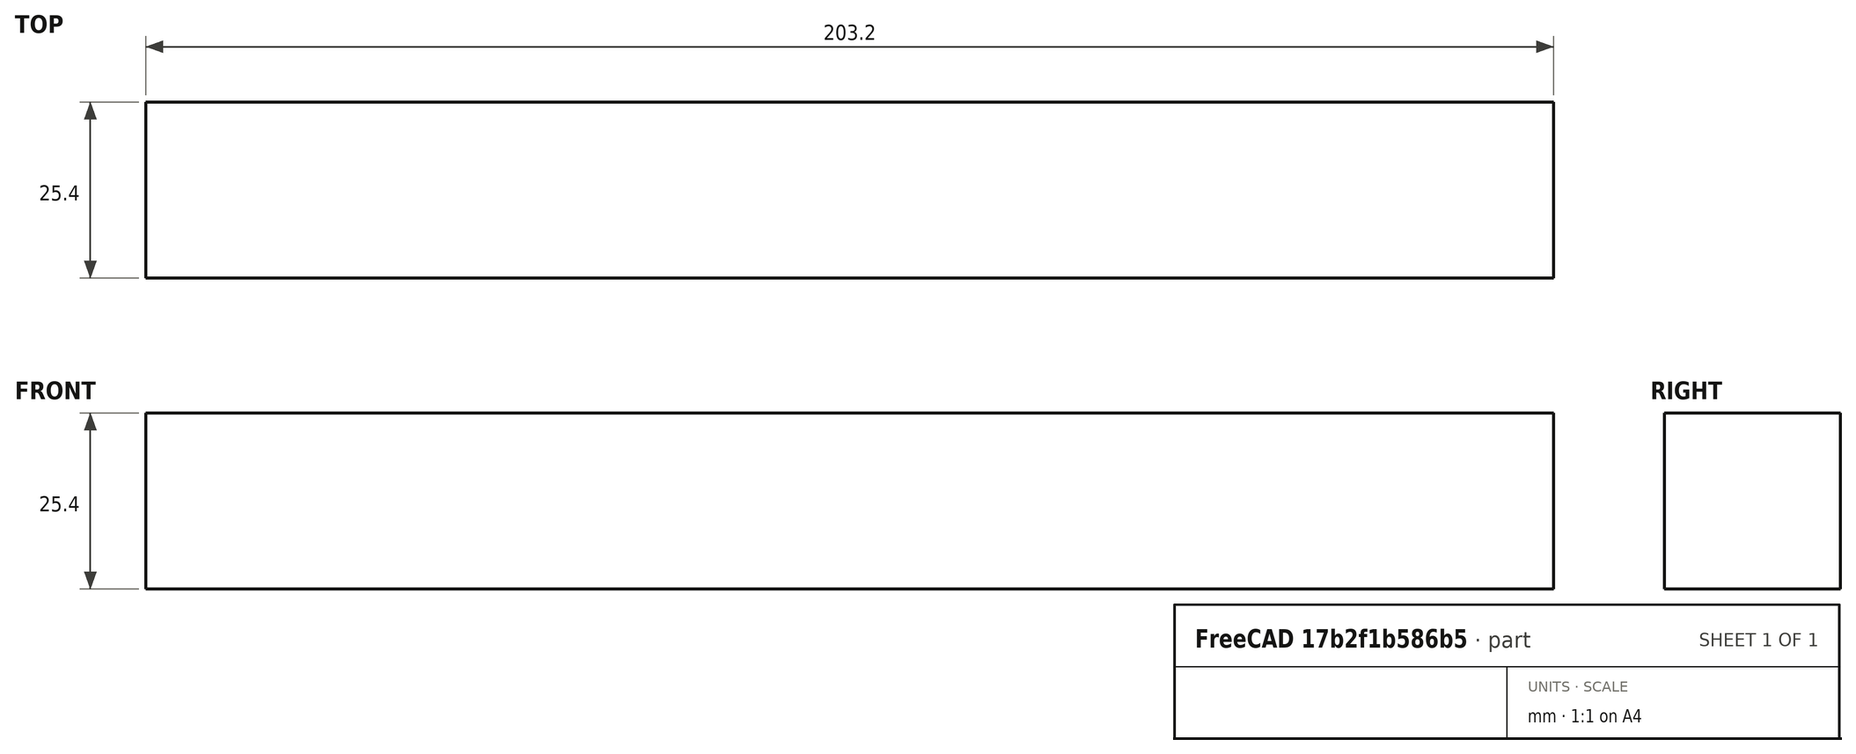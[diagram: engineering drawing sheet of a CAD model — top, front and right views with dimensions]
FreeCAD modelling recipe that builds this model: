
FCSTD DOCUMENT  (FreeCAD 0.17R10699 (Git))
Label: spine_thermomech
License: All rights reserved
LicenseURL: http://en.wikipedia.org/wiki/All_rights_reserved
objects: Part::Box×1, Fem::FemSolverObjectPython×1, Fem::FemMeshObject×1, App::MaterialObjectPython×1, Fem::ConstraintFixed×1, Fem::ConstraintInitialTemperature×1, Fem::ConstraintTemperature×1, Fem::ConstraintHeatflux×1, Fem::FemResultObjectPython×1, Fem::FemAnalysisPython×1
note: 1 computed .brp shape members not serialized (recipe doc carries the construction recipe); baked Part::Feature solids carry a one-line shape summary decoded from their .brp

FEATURE [Part::Box] Box
  AttacherType = Attacher::AttachEngine3D
  Height = 25.4
  Length = 203.2
  Width = 25.4
FEATURE [Fem::FemSolverObjectPython] CalculiX  # FEM object (typed FeaturePython)
  AnalysisType = 2
  EigenmodeHighLimit = 1000
  EigenmodeLowLimit = 0.5
  EigenmodesCount = 15
  GeometricalNonlinearity = 0
  IterationsControlParameterCutb = 0.25,0.5,0.75,0.85,,,1.5,
  IterationsControlParameterIter = 4,8,9,200,10,400,,200,,
  IterationsControlParameterTimeUse = true
  IterationsThermoMechMaximum = 2000
  IterationsUserDefinedIncrementations = false
  IterationsUserDefinedTimeStepLength = 0.1, 1.0
  MaterialNonlinearity = 0
  MatrixSolverType = 0
  SolverType = FemSolverCalculix
  SplitInputWriter = false
  ThermoMechSteadyState = true
  TimeEnd = 1
  TimeInitialStep = 1
FEATURE [Fem::FemMeshObject] Mesh
FEATURE [App::MaterialObjectPython] MechanicalMaterial  # material (typed FeaturePython)
  Category = 0
  Material = Density=7900 kg/m^3,Name=Steel-Generic,PoissonRatio=0.30,SpecificHeat=500 J/kg/K,ThermalConductivity=43.27 W/m/K,+2 more (map truncated)
FEATURE [Fem::ConstraintFixed] FemConstraintFixed
  NormalDirection = (-1,0,0)
  Normals = (16) [(-1,0,0),(-1,0,0),(-1,0,0),(-1,0,0),(-1,0,0),(-1,0,0),(-1,0,0),(-1,0,0),(-1,0,0),(-1,0,0),(-1,0,0),(-1,0,0),(-1,0,0),(-1,0,0),(-1,0,0),(-1,0,0)]
  Points = (16) [(0,25.4,0),(0,25.4,8.46667),(0,25.4,16.9333),(0,25.4,25.4),(0,16.9333,0),(0,16.9333,8.46667),(0,16.9333,16.9333),(0,16.9333,25.4),(0,8.46667,0),+7 more]
  References = -> [Box]
FEATURE [Fem::ConstraintInitialTemperature] FemConstraintInitialTemperature
  NormalDirection = (0,0,1)
  initialTemperature = 300
FEATURE [Fem::ConstraintTemperature] FemConstraintTemperature
  CFlux = 0
  ConstraintType = 1
  NormalDirection = (-1,0,0)
  Normals = (16) [(-1,0,0),(-1,0,0),(-1,0,0),(-1,0,0),(-1,0,0),(-1,0,0),(-1,0,0),(-1,0,0),(-1,0,0),(-1,0,0),(-1,0,0),(-1,0,0),(-1,0,0),(-1,0,0),(-1,0,0),(-1,0,0)]
  Points = (16) [(0,25.4,0),(0,25.4,8.46667),(0,25.4,16.9333),(0,25.4,25.4),(0,16.9333,0),(0,16.9333,8.46667),(0,16.9333,16.9333),(0,16.9333,25.4),(0,8.46667,0),+7 more]
  References = -> [Box]
  Temperature = 310.93
FEATURE [Fem::ConstraintHeatflux] FemConstraintHeatflux
  AmbientTemp = 255.372
  ConstraintType = 1
  DFlux = 0
  FilmCoef = 5.678
  NormalDirection = (0,-1,0)
  Normals = (64) [(0,-1,0),(0,-1,0),(0,-1,0),(0,-1,0),(0,-1,0),(0,-1,0),(0,-1,0),(0,-1,0),(0,-1,0),(0,-1,0),(0,-1,0),(0,-1,0),(0,-1,0),(0,-1,0),(0,-1,0),(0,-1,0),+48 more]
  Points = (64) [(0,0,0),(0,0,8.46667),(0,0,16.9333),(0,0,25.4),(67.7333,0,0),(67.7333,0,8.46667),(67.7333,0,16.9333),(67.7333,0,25.4),(135.467,0,0),+55 more]
  References = -> [Box]
  Scale = 11
FEATURE [Fem::FemResultObjectPython] CalculiX_thermomech_results  # FEM object (typed FeaturePython)
  DisplacementLengths = [0.00167108,0.0024824,0.00107755,0.00186939,0,0,0,0,0.00681127,0.00647907,0.00661732,0.00613781,0,0.00582005,0.00418411,0.00189581,0.00662788,0.00374675,0,0.00650644,0.00378478,0.0009262,0.00732571,0.0033935,0.00179715,0,0.00109313,0,0,+16 more]
  DisplacementVectors = (45) [(-0.000352892,-0.00160726,0.000290995),(0.000241406,-0.00163382,-0.00185329),(-0.000942455,0.00044281,0.00027714),+42 more]
  Eigenmode = 0
  EigenmodeFrequency = 0
  MaxShear = [0.309833,0.168182,0.472147,0.32241,15.4529,9.03465,18.1004,15.3132,0.781265,2.33473,2.32084,5.14995,14.7282,2.91877,0.45032,0.376204,4.16462,0.382447,17.032,4.1618,0.310077,0.482185,2.15922,0.408214,0.327898,14.8602,0.492202,17.4632,+17 more]
  Mesh = -> Mesh
  NodeNumbers = [1,2,3,4,5,6,7,8,9,10,11,12,13,14,15,16,17,18,19,20,21,22,23,24,25,26,27,28,29,30,31,32,33,34,35,36,37,38,39,40,41,42,43,44,45]
  PrincipalMax = [0.147958,0.677874,0.21448,0.0893159,-0.336996,0.461239,-0.230292,-0.432617,1.0544,3.2667,3.21831,10.9205,-2.77169,7.19338,0.916598,0.135795,3.51565,0.770133,-3.51068,3.53785,0.769957,0.108407,10.7922,0.79178,0.175789,-2.71318,0.138835,+18 more]
  PrincipalMed = [-0.192744,0.606999,0.0616273,-0.089708,-21.1449,-17.4651,-35.7433,-21.4738,0.309031,0.343445,0.406666,10.9098,-22.7115,3.89364,0.333515,-0.254772,0.340153,0.367389,-37.5063,0.235825,0.287053,-0.167392,7.7181,0.336805,-0.218753,-22.5044,+19 more]
  PrincipalMin = [-0.471708,0.34151,-0.729815,-0.555504,-31.2429,-17.6081,-36.431,-31.059,-0.508132,-1.40276,-1.42336,0.620557,-32.2281,1.35585,0.0159581,-0.616612,-4.81359,0.00523865,-37.5747,-4.78575,0.149804,-0.855964,6.47377,-0.0246472,-0.480008,+20 more]
  ResultType = FemResultMechanical
  Stats = [-0.000942455,0.00305855,0.00729818,-0.00163382,0.000616589,0.00222318,-0.00185329,0.000543914,0.00220675,0,0.00364478,0.00732571,0.307123,7.74746,35.8618,-5.82387,1.31924,10.9205,-37.7671,-4.87764,10.9098,-39.3672,-7.02358,6.47377,0.168182,+5 more]
  StressValues = [0.537534,0.307123,0.877906,0.576545,27.2957,17.9982,35.8618,27.1347,1.35367,4.08647,4.04966,10.2946,26.0369,5.06979,0.791195,0.651762,7.28083,0.662729,34.0299,7.25954,0.564191,0.860292,3.85016,0.708591,0.571833,26.2067,0.869544,33.9903,+17 more]
  StressVectors = (45) [(-0.453738,0.0373536,-0.100109),(0.676163,0.557167,0.393053),(-0.694336,0.121406,0.119222),(-0.48642,-0.0913616,0.0218851),+41 more]
  Temperature = [293.448,293.45,293.447,293.448,310.93,310.93,310.93,310.93,297.847,297.499,297.85,297.5,310.93,303.172,294.529,293.481,302.885,294.442,310.93,303.166,294.529,293.479,302.896,294.443,293.481,310.93,293.479,310.93,310.93,302.924,297.706,+14 more]
  Time = 1
FEATURE [Fem::FemAnalysisPython] Analysis  # FEM object (typed FeaturePython)
  Member = -> [CalculiX,Mesh,MechanicalMaterial,FemConstraintFixed,FemConstraintInitialTemperature,FemConstraintTemperature,FemConstraintHeatflux,CalculiX_thermomech_results]
